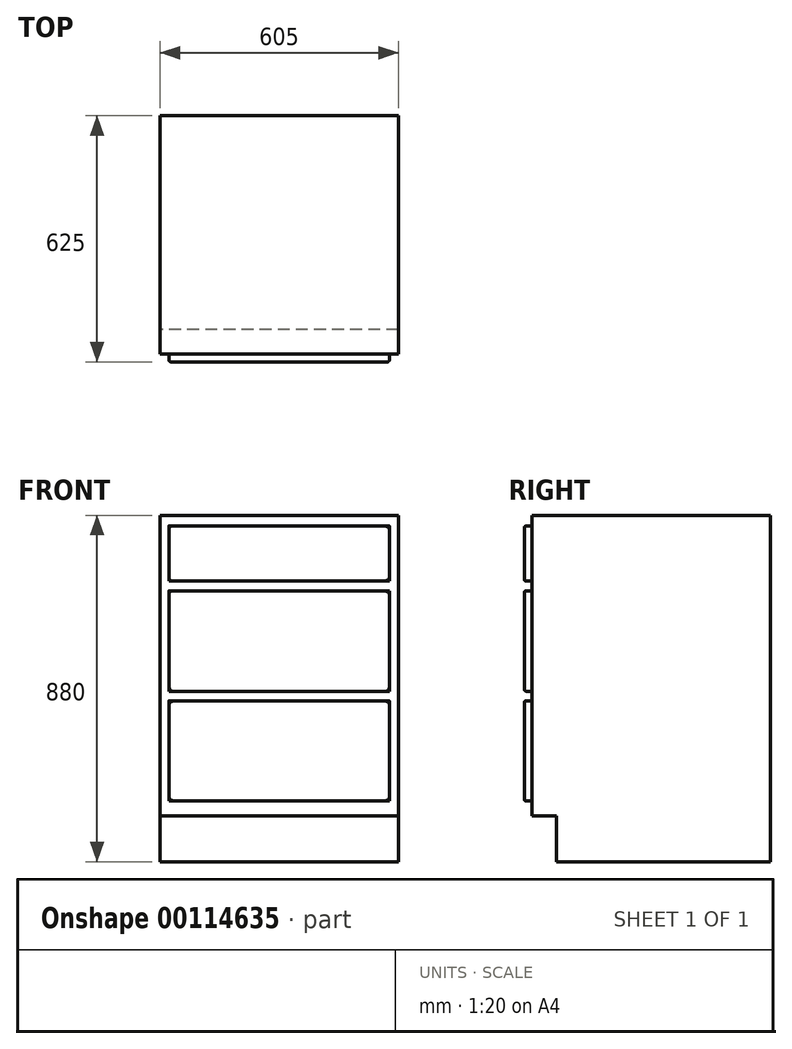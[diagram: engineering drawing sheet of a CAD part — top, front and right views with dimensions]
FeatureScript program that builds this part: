
annotation { "Feature Type Name" : "Feature", "Feature Type Description" : "" }
export const myFeature = defineFeature(function(context is Context, id is Id, definition is map)
    precondition{}
    {
        {
            var Q0;
            Q0=qCreatedBy(makeId("Front.planeOp"),FACE);
            var sketch = newSketch(context, id + "F0", { "sketchPlane" : qUnion([Q0])});
            skLineSegment(sketch, "E0.bottom", {"start": v(302.5, -440) * mm, "end": v(-302.5, -440) * mm});
            skLineSegment(sketch, "E0.top", {"start": v(302.5, 440) * mm, "end": v(-302.5, 440) * mm});
            skLineSegment(sketch, "E0.left", {"start": v(302.5, -440) * mm, "end": v(302.5, 440) * mm});
            skLineSegment(sketch, "E0.right", {"start": v(-302.5, -440) * mm, "end": v(-302.5, 440) * mm});
            skPoint(sketch, "E0.middle", {"position": v(0, 0) * mm});
            skSolve(sketch);
        }
        {
            var Q0;
            Q0=makeQuery(id+"F0.imprint","IMPRINT",FACE,{"disambiguationData":[TD([[makeQuery(id+"F0.imprint","IMPRINT",EDGE,{"derivedFrom":sQuery(id+"F0.wireOp",EDGE,"E0.bottom")}),-1.0]])]});
            extrude(context, id + "F1", {"entities" : qUnion([Q0]), "depth" : 605 * mm});
        }
        {
            var Q0;
            Q0=makeQuery(id+"F1.opExtrude","CAP_FACE",FACE,{"disambiguationData":[OSD([sQuery(id+"F0.wireOp",EDGE,"E0.bottom"),sQuery(id+"F0.wireOp",EDGE,"E0.top"),sQuery(id+"F0.wireOp",EDGE,"E0.left"),sQuery(id+"F0.wireOp",EDGE,"E0.right")])],"isStart":false});
            var sketch = newSketch(context, id + "F2", { "sketchPlane" : qUnion([Q0])});
            skLineSegment(sketch, "E1.bottom", {"start": v(-302.5, -440) * mm, "end": v(302.5, -440) * mm});
            skLineSegment(sketch, "E1.top", {"start": v(-302.5, -324) * mm, "end": v(302.5, -324) * mm});
            skLineSegment(sketch, "E1.left", {"start": v(-302.5, -440) * mm, "end": v(-302.5, -324) * mm});
            skLineSegment(sketch, "E1.right", {"start": v(302.5, -440) * mm, "end": v(302.5, -324) * mm});
            skSolve(sketch);
        }
        {
            var Q0;
            Q0=makeQuery(id+"F2.imprint","IMPRINT",FACE,{"disambiguationData":[TD([[makeQuery(id+"F2.imprint","IMPRINT",EDGE,{"derivedFrom":sQuery(id+"F2.wireOp",EDGE,"E1.bottom")}),-1.0]])]});
            extrude(context, id + "F3", {"entities" : qUnion([Q0]), "operationType" : NewBodyOperationType.REMOVE, "oppositeDirection" : true, "depth" : 62 * mm});
        }
        {
            var Q0;
            Q0=makeQuery(id+"F1.opExtrude","CAP_FACE",FACE,{"disambiguationData":[OSD([sQuery(id+"F0.wireOp",EDGE,"E0.bottom"),sQuery(id+"F0.wireOp",EDGE,"E0.top"),sQuery(id+"F0.wireOp",EDGE,"E0.left"),sQuery(id+"F0.wireOp",EDGE,"E0.right")])],"isStart":false});
            var sketch = newSketch(context, id + "F4", { "sketchPlane" : qUnion([Q0])});
            skLineSegment(sketch, "E2.bottom", {"start": v(280, 273) * mm, "end": v(-280, 273) * mm});
            skLineSegment(sketch, "E2.top", {"start": v(280, 413) * mm, "end": v(-280, 413) * mm});
            skLineSegment(sketch, "E2.left", {"start": v(280, 273) * mm, "end": v(280, 413) * mm});
            skLineSegment(sketch, "E2.right", {"start": v(-280, 273) * mm, "end": v(-280, 413) * mm});
            skPoint(sketch, "E2.middle", {"position": v(0, 343) * mm});
            skSolve(sketch);
        }
        {
            var Q0;
            Q0=makeQuery(id+"F4.imprint","IMPRINT",FACE,{"disambiguationData":[TD([[makeQuery(id+"F4.imprint","IMPRINT",EDGE,{"derivedFrom":sQuery(id+"F4.wireOp",EDGE,"E2.bottom")}),-1.0]])]});
            extrude(context, id + "F5", {"entities" : qUnion([Q0]), "operationType" : NewBodyOperationType.ADD, "depth" : 20 * mm});
        }
        {
            var Q0;
            Q0=makeQuery(id+"F1.opExtrude","CAP_FACE",FACE,{"disambiguationData":[OSD([sQuery(id+"F0.wireOp",EDGE,"E0.bottom"),sQuery(id+"F0.wireOp",EDGE,"E0.top"),sQuery(id+"F0.wireOp",EDGE,"E0.left"),sQuery(id+"F0.wireOp",EDGE,"E0.right")])],"isStart":false});
            var sketch = newSketch(context, id + "F6", { "sketchPlane" : qUnion([Q0])});
            skLineSegment(sketch, "E3.bottom", {"start": v(280, -7) * mm, "end": v(-280, -7) * mm});
            skLineSegment(sketch, "E3.top", {"start": v(280, 248) * mm, "end": v(-280, 248) * mm});
            skLineSegment(sketch, "E3.left", {"start": v(280, -7) * mm, "end": v(280, 248) * mm});
            skLineSegment(sketch, "E3.right", {"start": v(-280, -7) * mm, "end": v(-280, 248) * mm});
            skPoint(sketch, "E3.middle", {"position": v(0, 120.5) * mm});
            skSolve(sketch);
        }
        {
            var Q0;
            Q0=qSketchRegion(id+"F6",true);
            extrude(context, id + "F7", {"entities" : qUnion([Q0]), "operationType" : NewBodyOperationType.ADD, "depth" : 20 * mm});
        }
        {
            var Q0;
            Q0=makeQuery(id+"F1.opExtrude","CAP_FACE",FACE,{"disambiguationData":[OSD([sQuery(id+"F0.wireOp",EDGE,"E0.bottom"),sQuery(id+"F0.wireOp",EDGE,"E0.top"),sQuery(id+"F0.wireOp",EDGE,"E0.left"),sQuery(id+"F0.wireOp",EDGE,"E0.right")])],"isStart":false});
            var sketch = newSketch(context, id + "F8", { "sketchPlane" : qUnion([Q0])});
            skLineSegment(sketch, "E4.bottom", {"start": v(280, -286) * mm, "end": v(-280, -286) * mm});
            skLineSegment(sketch, "E4.top", {"start": v(280, -31) * mm, "end": v(-280, -31) * mm});
            skLineSegment(sketch, "E4.left", {"start": v(280, -286) * mm, "end": v(280, -31) * mm});
            skLineSegment(sketch, "E4.right", {"start": v(-280, -286) * mm, "end": v(-280, -31) * mm});
            skPoint(sketch, "E4.middle", {"position": v(0, -158.5) * mm});
            skSolve(sketch);
        }
        {
            var Q0;
            Q0=makeQuery(id+"F8.imprint","IMPRINT",FACE,{"disambiguationData":[TD([[makeQuery(id+"F8.imprint","IMPRINT",EDGE,{"derivedFrom":sQuery(id+"F8.wireOp",EDGE,"E4.bottom")}),-1.0]])]});
            extrude(context, id + "F9", {"entities" : qUnion([Q0]), "operationType" : NewBodyOperationType.ADD, "depth" : 20 * mm});
        }
        {
            var Q0;
            Q0=makeQuery(id+"F5.opExtrude","CAP_EDGE",EDGE,{"disambiguationData":[OSD([sQuery(id+"F4.wireOp",EDGE,"E2.top")])],"isStart":false});
            var Q1;
            Q1=makeQuery(id+"F5.opExtrude","CAP_EDGE",EDGE,{"disambiguationData":[OSD([sQuery(id+"F4.wireOp",EDGE,"E2.right")])],"isStart":false});
            var Q2;
            Q2=makeQuery(id+"F5.opExtrude","CAP_EDGE",EDGE,{"disambiguationData":[OSD([sQuery(id+"F4.wireOp",EDGE,"E2.bottom")])],"isStart":false});
            var Q3;
            Q3=makeQuery(id+"F5.opExtrude","CAP_EDGE",EDGE,{"disambiguationData":[OSD([sQuery(id+"F4.wireOp",EDGE,"E2.left")])],"isStart":false});
            var Q4;
            Q4=makeQuery(id+"F7.opExtrude","CAP_EDGE",EDGE,{"disambiguationData":[OSD([sQuery(id+"F6.wireOp",EDGE,"E3.top")])],"isStart":false});
            var Q5;
            Q5=makeQuery(id+"F7.opExtrude","CAP_EDGE",EDGE,{"disambiguationData":[OSD([sQuery(id+"F6.wireOp",EDGE,"E3.left")])],"isStart":false});
            var Q6;
            Q6=makeQuery(id+"F7.opExtrude","CAP_EDGE",EDGE,{"disambiguationData":[OSD([sQuery(id+"F6.wireOp",EDGE,"E3.right")])],"isStart":false});
            var Q7;
            Q7=makeQuery(id+"F7.opExtrude","CAP_EDGE",EDGE,{"disambiguationData":[OSD([sQuery(id+"F6.wireOp",EDGE,"E3.bottom")])],"isStart":false});
            var Q8;
            Q8=makeQuery(id+"F9.opExtrude","CAP_EDGE",EDGE,{"disambiguationData":[OSD([sQuery(id+"F8.wireOp",EDGE,"E4.top")])],"isStart":false});
            var Q9;
            Q9=makeQuery(id+"F9.opExtrude","CAP_EDGE",EDGE,{"disambiguationData":[OSD([sQuery(id+"F8.wireOp",EDGE,"E4.right")])],"isStart":false});
            var Q10;
            Q10=makeQuery(id+"F9.opExtrude","CAP_EDGE",EDGE,{"disambiguationData":[OSD([sQuery(id+"F8.wireOp",EDGE,"E4.bottom")])],"isStart":false});
            var Q11;
            Q11=makeQuery(id+"F9.opExtrude","CAP_EDGE",EDGE,{"disambiguationData":[OSD([sQuery(id+"F8.wireOp",EDGE,"E4.left")])],"isStart":false});
            fillet(context, id + "F10", {"entities" : qUnion([Q0, Q1, Q2, Q3, Q4, Q5, Q6, Q7, Q8, Q9, Q10, Q11]), "radius" : 5.08 * mm, "tangentPropagation" : true, "allowEdgeOverflow" : false});
        }
    });
